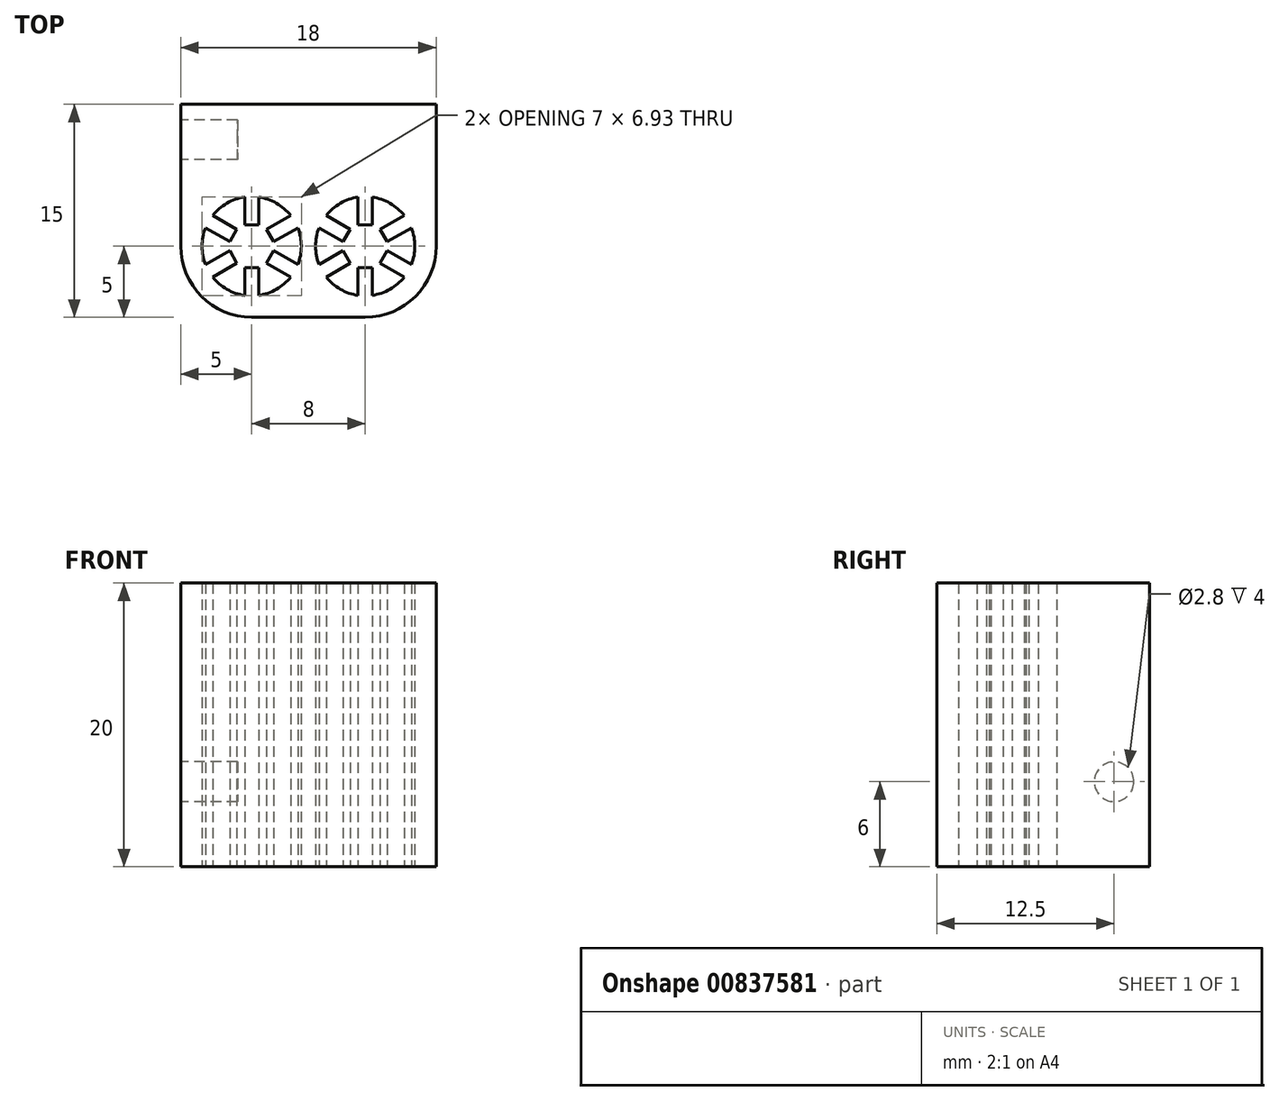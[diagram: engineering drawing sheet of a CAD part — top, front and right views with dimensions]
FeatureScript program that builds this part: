
annotation { "Feature Type Name" : "Feature", "Feature Type Description" : "" }
export const myFeature = defineFeature(function(context is Context, id is Id, definition is map)
    precondition{}
    {
        {
            var Q0;
            Q0=qCreatedBy(makeId("Top.planeOp"),FACE);
            var sketch = newSketch(context, id + "F0", { "sketchPlane" : qUnion([Q0])});
            skCircle(sketch, "E0", {"center": v(0, 0) * mm, "radius": 1.5 * mm, "construction": true});
            skArc(sketch, "E1", {"start": v(-0.5, 3.46) * mm, "mid": v(-1.75, 3.03) * mm, "end": v(-2.75, 2.17) * mm});
            skLineSegment(sketch, "E2.top", {"start": v(-0.5, 1.5) * mm, "end": v(0.5, 1.5) * mm});
            skLineSegment(sketch, "E2.left", {"start": v(-0.5, 3.46) * mm, "end": v(-0.5, 1.5) * mm});
            skLineSegment(sketch, "E2.right", {"start": v(0.5, 3.46) * mm, "end": v(0.5, 1.5) * mm});
            skLineSegment(sketch, "E3", {"start": v(0, 0) * mm, "end": v(0, 4.33) * mm, "construction": true});
            skLineSegment(sketch, "E4.1.0", {"start": v(-3.25, 1.3) * mm, "end": v(-1.55, 0.32) * mm});
            skLineSegment(sketch, "E4.1.1", {"start": v(-1.55, 0.32) * mm, "end": v(-1.05, 1.18) * mm});
            skLineSegment(sketch, "E4.1.2", {"start": v(-2.75, 2.17) * mm, "end": v(-1.05, 1.18) * mm});
            skLineSegment(sketch, "E4.2.0", {"start": v(-2.75, -2.17) * mm, "end": v(-1.05, -1.18) * mm});
            skLineSegment(sketch, "E4.2.1", {"start": v(-1.05, -1.18) * mm, "end": v(-1.55, -0.32) * mm});
            skLineSegment(sketch, "E4.2.2", {"start": v(-3.25, -1.3) * mm, "end": v(-1.55, -0.32) * mm});
            skLineSegment(sketch, "E5.2.3.0", {"start": v(0.5, -3.46) * mm, "end": v(0.5, -1.5) * mm});
            skLineSegment(sketch, "E5.3.3.0", {"start": v(0.5, -1.5) * mm, "end": v(-0.5, -1.5) * mm});
            skLineSegment(sketch, "E5.6.3.0", {"start": v(-0.5, -3.46) * mm, "end": v(-0.5, -1.5) * mm});
            skLineSegment(sketch, "E5.2.4.0", {"start": v(3.25, -1.3) * mm, "end": v(1.55, -0.32) * mm});
            skLineSegment(sketch, "E5.3.4.0", {"start": v(1.55, -0.32) * mm, "end": v(1.05, -1.18) * mm});
            skLineSegment(sketch, "E5.6.4.0", {"start": v(2.75, -2.17) * mm, "end": v(1.05, -1.18) * mm});
            skLineSegment(sketch, "E5.2.5.0", {"start": v(2.75, 2.17) * mm, "end": v(1.05, 1.18) * mm});
            skLineSegment(sketch, "E5.3.5.0", {"start": v(1.05, 1.18) * mm, "end": v(1.55, 0.32) * mm});
            skLineSegment(sketch, "E5.6.5.0", {"start": v(3.25, 1.3) * mm, "end": v(1.55, 0.32) * mm});
            skArc(sketch, "E6.trimOffspring", {"start": v(-3.25, 1.3) * mm, "mid": v(-3.5, 0) * mm, "end": v(-3.25, -1.3) * mm});
            skArc(sketch, "E7.trimOffspring", {"start": v(-2.75, -2.17) * mm, "mid": v(-1.75, -3.03) * mm, "end": v(-0.5, -3.46) * mm});
            skArc(sketch, "E8.trimOffspring", {"start": v(0.5, -3.46) * mm, "mid": v(1.75, -3.03) * mm, "end": v(2.75, -2.17) * mm});
            skArc(sketch, "E9.trimOffspring", {"start": v(3.25, -1.3) * mm, "mid": v(3.5, 0) * mm, "end": v(3.25, 1.3) * mm});
            skArc(sketch, "E10.trimOffspring", {"start": v(2.75, 2.17) * mm, "mid": v(0, 3.5) * mm, "end": v(-2.75, 2.17) * mm});
            skArc(sketch, "E11.trimOffspring", {"start": v(2.75, 2.17) * mm, "mid": v(1.75, 3.03) * mm, "end": v(0.5, 3.46) * mm});
            skCircle(sketch, "E12", {"center": v(-8, 0) * mm, "radius": 1.5 * mm, "construction": true});
            skArc(sketch, "E13", {"start": v(-8.5, 3.46) * mm, "mid": v(-9.75, 3.03) * mm, "end": v(-10.75, 2.17) * mm});
            skLineSegment(sketch, "E14.top", {"start": v(-8.5, 1.5) * mm, "end": v(-7.5, 1.5) * mm});
            skLineSegment(sketch, "E14.left", {"start": v(-8.5, 3.46) * mm, "end": v(-8.5, 1.5) * mm});
            skLineSegment(sketch, "E14.right", {"start": v(-7.5, 3.46) * mm, "end": v(-7.5, 1.5) * mm});
            skLineSegment(sketch, "E15", {"start": v(-8, 0) * mm, "end": v(-8, 4.05) * mm, "construction": true});
            skLineSegment(sketch, "E16.1.0", {"start": v(-11.25, 1.3) * mm, "end": v(-9.55, 0.32) * mm});
            skLineSegment(sketch, "E16.1.1", {"start": v(-9.55, 0.32) * mm, "end": v(-9.05, 1.18) * mm});
            skLineSegment(sketch, "E16.1.2", {"start": v(-10.75, 2.17) * mm, "end": v(-9.05, 1.18) * mm});
            skLineSegment(sketch, "E16.2.0", {"start": v(-10.75, -2.17) * mm, "end": v(-9.05, -1.18) * mm});
            skLineSegment(sketch, "E16.2.1", {"start": v(-9.05, -1.18) * mm, "end": v(-9.55, -0.32) * mm});
            skLineSegment(sketch, "E16.2.2", {"start": v(-11.25, -1.3) * mm, "end": v(-9.55, -0.32) * mm});
            skLineSegment(sketch, "E17.2.3.0", {"start": v(-7.5, -3.46) * mm, "end": v(-7.5, -1.5) * mm});
            skLineSegment(sketch, "E17.3.3.0", {"start": v(-7.5, -1.5) * mm, "end": v(-8.5, -1.5) * mm});
            skLineSegment(sketch, "E17.6.3.0", {"start": v(-8.5, -3.46) * mm, "end": v(-8.5, -1.5) * mm});
            skLineSegment(sketch, "E17.2.4.0", {"start": v(-4.75, -1.3) * mm, "end": v(-6.45, -0.32) * mm});
            skLineSegment(sketch, "E17.3.4.0", {"start": v(-6.45, -0.32) * mm, "end": v(-6.95, -1.18) * mm});
            skLineSegment(sketch, "E17.6.4.0", {"start": v(-5.25, -2.17) * mm, "end": v(-6.95, -1.18) * mm});
            skLineSegment(sketch, "E17.2.5.0", {"start": v(-5.25, 2.17) * mm, "end": v(-6.95, 1.18) * mm});
            skLineSegment(sketch, "E17.3.5.0", {"start": v(-6.95, 1.18) * mm, "end": v(-6.45, 0.32) * mm});
            skLineSegment(sketch, "E17.6.5.0", {"start": v(-4.75, 1.3) * mm, "end": v(-6.45, 0.32) * mm});
            skArc(sketch, "E18.trimOffspring", {"start": v(-11.25, 1.3) * mm, "mid": v(-11.5, 0) * mm, "end": v(-11.25, -1.3) * mm});
            skArc(sketch, "E19.trimOffspring", {"start": v(-10.75, -2.17) * mm, "mid": v(-9.75, -3.03) * mm, "end": v(-8.5, -3.46) * mm});
            skArc(sketch, "E20.trimOffspring", {"start": v(-7.5, -3.46) * mm, "mid": v(-6.25, -3.03) * mm, "end": v(-5.25, -2.17) * mm});
            skArc(sketch, "E21.trimOffspring", {"start": v(-4.75, -1.3) * mm, "mid": v(-4.5, 0) * mm, "end": v(-4.75, 1.3) * mm});
            skArc(sketch, "E22.trimOffspring", {"start": v(-5.25, 2.17) * mm, "mid": v(-8, 3.5) * mm, "end": v(-10.75, 2.17) * mm});
            skArc(sketch, "E23.trimOffspring", {"start": v(-5.25, 2.17) * mm, "mid": v(-6.25, 3.03) * mm, "end": v(-7.5, 3.46) * mm});
            skLineSegment(sketch, "E24", {"start": v(-13, 0) * mm, "end": v(5, 0) * mm, "construction": true});
            skArc(sketch, "E25", {"start": v(5, 0) * mm, "mid": v(3.54, -3.54) * mm, "end": v(0, -5) * mm});
            skArc(sketch, "E26", {"start": v(-8, -5) * mm, "mid": v(-11.54, -3.54) * mm, "end": v(-13, 0) * mm});
            skLineSegment(sketch, "E27", {"start": v(-8, -5) * mm, "end": v(0, -5) * mm});
            skLineSegment(sketch, "E28", {"start": v(-13, 10) * mm, "end": v(5, 10) * mm});
            skLineSegment(sketch, "E29", {"start": v(5, 10) * mm, "end": v(5, 0) * mm});
            skLineSegment(sketch, "E30", {"start": v(-13, 10) * mm, "end": v(-13, 0) * mm});
            skLineSegment(sketch, "E31", {"start": v(-4, -5) * mm, "end": v(-4, 10) * mm, "construction": true});
            skSolve(sketch);
        }
        {
            var Q0;
            Q0=makeQuery(id+"F0.imprint","IMPRINT",FACE,{"disambiguationData":[TD([[makeQuery(id+"F0.imprint","IMPRINT",EDGE,{"derivedFrom":sQuery(id+"F0.wireOp",EDGE,"bOMb4E9l-yj9f-PJcJ-j4vr-m1u1RJyjrOUS")}),1.0]])]});
            var Q1;
            {var subQ0=sQuery(id+"F0.wireOp",EDGE,"E4.1.0");Q1=makeQuery(id+"F0.imprint","IMPRINT",FACE,{"disambiguationData":[TD([[makeQuery(id+"F0.imprint","IMPRINT",EDGE,{"derivedFrom":subQ0}),1.0]])]});}
            var Q2;
            Q2=makeQuery(id+"F0.imprint","IMPRINT",FACE,{"disambiguationData":[TD([[makeQuery(id+"F0.imprint","IMPRINT",EDGE,{"derivedFrom":sQuery(id+"F0.wireOp",EDGE,"E2.top")}),1.0]])]});
            var Q3;
            {var subQ0=sQuery(id+"F0.wireOp",EDGE,"E4.2.0");Q3=makeQuery(id+"F0.imprint","IMPRINT",FACE,{"disambiguationData":[TD([[makeQuery(id+"F0.imprint","IMPRINT",EDGE,{"derivedFrom":subQ0}),1.0]])]});}
            var Q4;
            {var subQ0=sQuery(id+"F0.wireOp",EDGE,"E5.2.3.0");Q4=makeQuery(id+"F0.imprint","IMPRINT",FACE,{"disambiguationData":[TD([[makeQuery(id+"F0.imprint","IMPRINT",EDGE,{"derivedFrom":subQ0}),1.0]])]});}
            var Q5;
            {var subQ0=sQuery(id+"F0.wireOp",EDGE,"E5.2.4.0");Q5=makeQuery(id+"F0.imprint","IMPRINT",FACE,{"disambiguationData":[TD([[makeQuery(id+"F0.imprint","IMPRINT",EDGE,{"derivedFrom":subQ0}),1.0]])]});}
            var Q6;
            {var subQ0=sQuery(id+"F0.wireOp",EDGE,"RkvQvHyZ-bFmo-uS0o-NlfA-jaB9pi21HWwc");Q6=makeQuery(id+"F0.imprint","IMPRINT",FACE,{"disambiguationData":[TD([[makeQuery(id+"F0.imprint","IMPRINT",EDGE,{"derivedFrom":subQ0}),1.0]])]});}
            var Q7;
            Q7=makeQuery(id+"F0.imprint","IMPRINT",FACE,{"disambiguationData":[TD([[makeQuery(id+"F0.imprint","IMPRINT",EDGE,{"derivedFrom":sQuery(id+"F0.wireOp",EDGE,"E14.top")}),1.0]])]});
            extrude(context, id + "F1", {"entities" : qUnion([Q0, Q1, Q2, Q3, Q4, Q5, Q6, Q7]), "endBound" : BoundingType.SYMMETRIC, "depth" : 20 * mm, "offsetDistance" : 25 * mm});
        }
        {
            var Q0;
            Q0=makeQuery(id+"F1.opExtrude","SWEPT_FACE",FACE,{"disambiguationData":[OSD([sQuery(id+"F0.wireOp",EDGE,"E30")])]});
            var sketch = newSketch(context, id + "F2", { "sketchPlane" : qUnion([Q0])});
            skCircle(sketch, "E32", {"center": v(-7.5, -4) * mm, "radius": 1.4 * mm});
            skSolve(sketch);
        }
        {
            var Q0;
            Q0=makeQuery(id+"F2.imprint","IMPRINT",FACE,{"disambiguationData":[TD([[makeQuery(id+"F2.imprint","IMPRINT",EDGE,{"derivedFrom":sQuery(id+"F2.wireOp",EDGE,"E32")}),1.0]])]});
            extrude(context, id + "F3", {"entities" : qUnion([Q0]), "operationType" : NewBodyOperationType.REMOVE, "oppositeDirection" : true, "depth" : 4 * mm, "offsetDistance" : 25 * mm});
        }
    });
